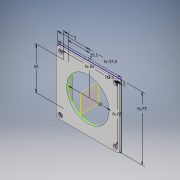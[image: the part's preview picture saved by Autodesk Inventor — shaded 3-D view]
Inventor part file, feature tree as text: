
AUTODESK INVENTOR PART (.ipt)
format: ipt  version: 2019 (Build 230136000, 136)  size: 160,256 bytes
history: native  units: mm
features: extrude x2, fillet x2, sketch x1, plane x1, mirror x1
ambient origin geometry x8: Origin, YZ Plane, XZ Plane, XY Plane, X Axis, Y Axis, Z Axis, Center Point
bodies: Solid1 (feature_tree)
feature tree (7):
  sketch  "Sketch1"  dims[d0=75.0mm d1=75.0mm d2=5.3mm d3=5.0mm d4=5.0mm d5=20.0mm d7=65.0mm d8=20.0mm d10=65.0mm d15=2.0mm d16=0.0mm d19=5.0mm d20=0.0mm d26=50.0mm d29=50.0mm d30=5.0mm d31=25.5mm d32=37.5mm d33=4.0mm d35=4.0mm]
  extrude  "Extrusion1"  Depth=75.0mm
  extrude  "Extrusion2"  Depth=4.0mm
  plane  "Work Plane1"
  mirror  "Mirror1"
  fillet  "Fillet2"  Radius=5.0mm
  fillet  "Fillet3"  Radius=5.0mm
